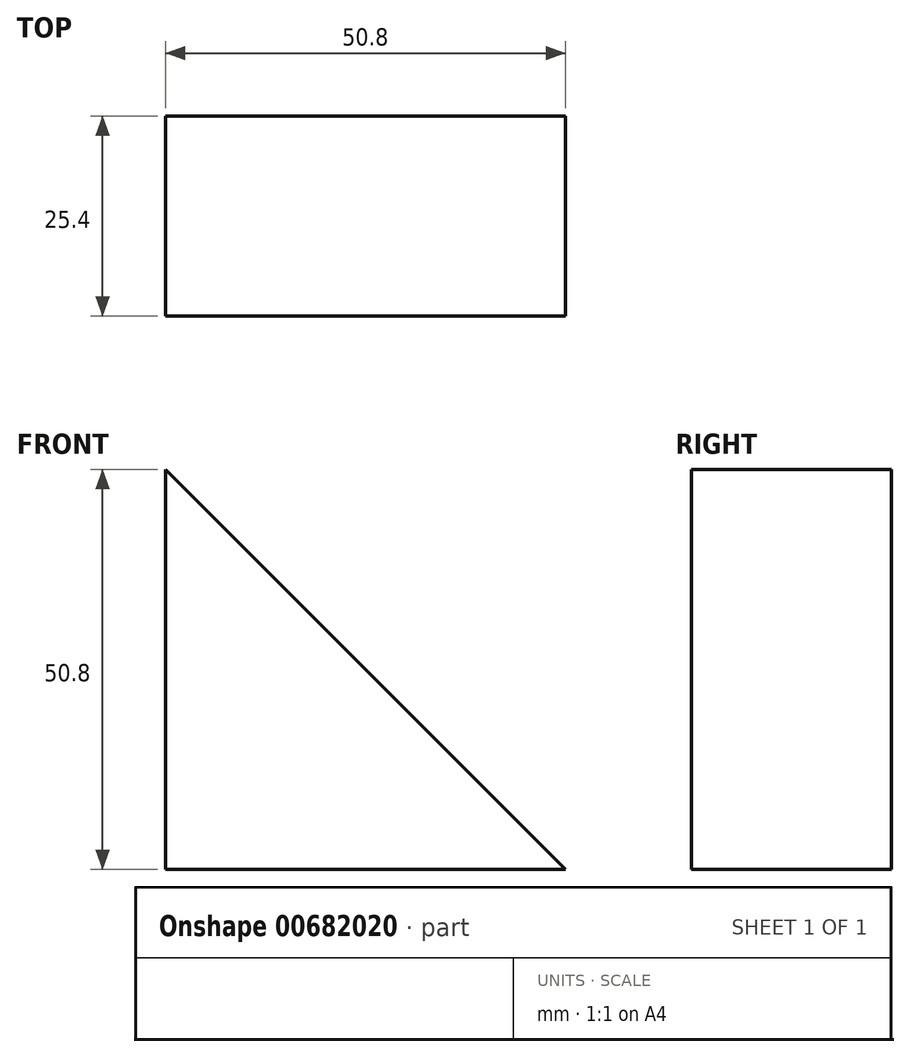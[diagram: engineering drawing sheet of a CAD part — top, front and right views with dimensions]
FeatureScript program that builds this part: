
annotation { "Feature Type Name" : "Feature", "Feature Type Description" : "" }
export const myFeature = defineFeature(function(context is Context, id is Id, definition is map)
    precondition{}
    {
        {
            var Q0;
            Q0=qCreatedBy(makeId("Front.planeOp"),FACE);
            var sketch = newSketch(context, id + "F0", { "sketchPlane" : qUnion([Q0])});
            skLineSegment(sketch, "E0", {"start": v(-50.8, 50.8) * mm, "end": v(-50.8, 0) * mm});
            skLineSegment(sketch, "E1", {"start": v(-50.8, 0) * mm, "end": v(0, 0) * mm});
            skLineSegment(sketch, "E2", {"start": v(0, 0) * mm, "end": v(-50.8, 50.8) * mm});
            skSolve(sketch);
        }
        {
            var Q0;
            Q0 = qSketchRegion(id + "F0", true);
            extrude(context, id + "F1", {"entities" : qUnion([Q0]), "depth" : 25.4 * mm, "offsetDistance" : 25.4 * mm});
        }
    });
